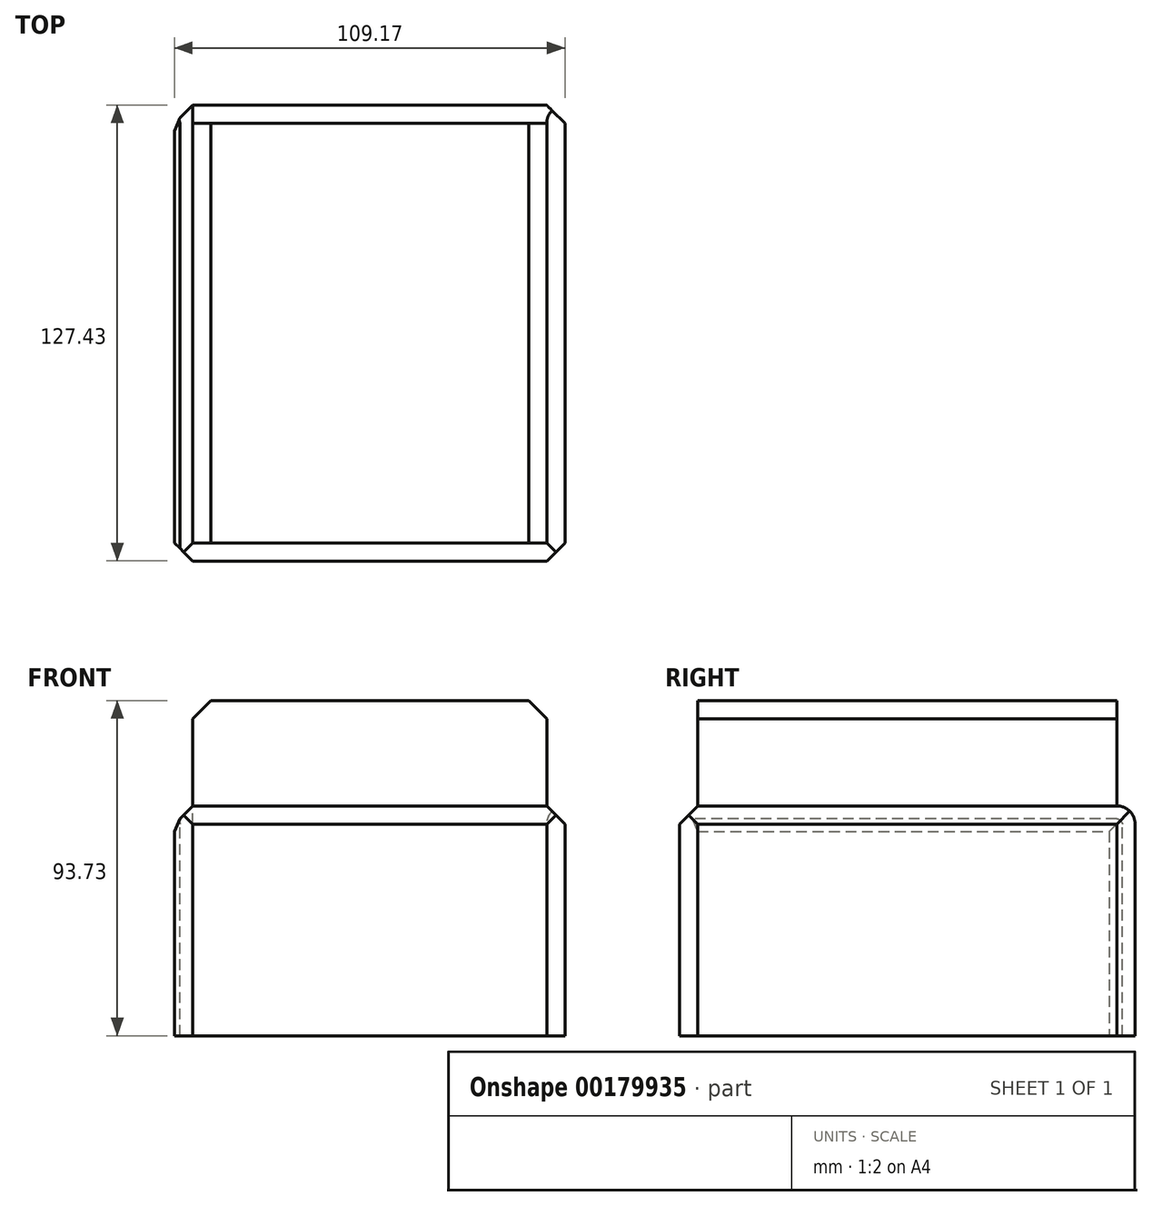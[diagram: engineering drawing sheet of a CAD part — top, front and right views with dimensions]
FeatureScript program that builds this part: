
annotation { "Feature Type Name" : "Feature", "Feature Type Description" : "" }
export const myFeature = defineFeature(function(context is Context, id is Id, definition is map)
    precondition{}
    {
        {
            var Q0;
            Q0=qCreatedBy(makeId("Top.planeOp"),FACE);
            var sketch = newSketch(context, id + "F0", { "sketchPlane" : qUnion([Q0])});
            skLineSegment(sketch, "E0.bottom", {"start": v(-52.1, 63.82) * mm, "end": v(57.08, 63.82) * mm});
            skLineSegment(sketch, "E0.top", {"start": v(-52.1, -63.61) * mm, "end": v(57.08, -63.61) * mm});
            skLineSegment(sketch, "E0.left", {"start": v(-52.1, 63.82) * mm, "end": v(-52.1, -63.61) * mm});
            skLineSegment(sketch, "E0.right", {"start": v(57.08, 63.82) * mm, "end": v(57.08, -63.61) * mm});
            skSolve(sketch);
        }
        {
            var Q0;
            Q0=makeQuery(id+"F0.imprint","IMPRINT",FACE,{"disambiguationData":[TD([[makeQuery(id+"F0.imprint","IMPRINT",EDGE,{"derivedFrom":sQuery(id+"F0.wireOp",EDGE,"E0.bottom")}),-1.0]])]});
            extrude(context, id + "F1", {"entities" : qUnion([Q0]), "depth" : 64.26 * mm});
        }
        {
            var Q0;
            Q0=makeQuery(id+"F1.opExtrude","CAP_EDGE",EDGE,{"disambiguationData":[OSD([sQuery(id+"F0.wireOp",EDGE,"E0.right")])],"isStart":false});
            chamfer(context, id + "F2", {"entities" : qUnion([Q0]), "width" : 5.08 * mm, "tangentPropagation" : true});
        }
        {
            var Q0;
            Q0=makeQuery(id+"F1.opExtrude","CAP_EDGE",EDGE,{"disambiguationData":[OSD([sQuery(id+"F0.wireOp",EDGE,"E0.bottom")])],"isStart":false});
            fillet(context, id + "F3", {"entities" : qUnion([Q0]), "radius" : 5.08 * mm, "tangentPropagation" : true, "allowEdgeOverflow" : false});
        }
        {
            var Q0;
            Q0=makeQuery(id+"F1.opExtrude","CAP_EDGE",EDGE,{"disambiguationData":[OSD([sQuery(id+"F0.wireOp",EDGE,"E0.top")])],"isStart":false});
            chamfer(context, id + "F4", {"entities" : qUnion([Q0]), "width" : 5.08 * mm, "tangentPropagation" : true});
        }
        {
            var Q0;
            Q0=makeQuery(id+"F1.opExtrude","CAP_EDGE",EDGE,{"disambiguationData":[OSD([sQuery(id+"F0.wireOp",EDGE,"E0.left")])],"isStart":false});
            chamfer(context, id + "F5", {"entities" : qUnion([Q0]), "width" : 5.08 * mm, "tangentPropagation" : true});
        }
        {
            var Q0;
            {var subQ0=sQuery(id+"F0.wireOp",EDGE,"E0.left");Q0=makeQuery(id+"F5.opChamfer","BLEND_EDGE",EDGE,{"blendedFrom":[makeQuery(id+"F1.opExtrude","SWEPT_EDGE",EDGE,{"disambiguationData":[OSD([sQuery(id+"F0.wireOp",EDGE,"E0.bottom"),subQ0])]}),makeQuery(id+"F1.opExtrude","SWEPT_FACE",FACE,{"disambiguationData":[OSD([subQ0])]})],"blendedInto":[makeQuery(id+"F1.opExtrude","SWEPT_FACE",FACE,{"disambiguationData":[OSD([subQ0])]})]});}
            chamfer(context, id + "F6", {"entities" : qUnion([Q0]), "width" : 5.08 * mm, "tangentPropagation" : true});
        }
        {
            var Q0;
            Q0=makeQuery(id+"F1.opExtrude","SWEPT_EDGE",EDGE,{"disambiguationData":[OSD([sQuery(id+"F0.wireOp",EDGE,"E0.top"),sQuery(id+"F0.wireOp",EDGE,"E0.left")])]});
            chamfer(context, id + "F7", {"entities" : qUnion([Q0]), "width" : 5.08 * mm, "tangentPropagation" : true});
        }
        {
            var Q0;
            Q0=makeQuery(id+"F1.opExtrude","SWEPT_EDGE",EDGE,{"disambiguationData":[OSD([sQuery(id+"F0.wireOp",EDGE,"E0.top"),sQuery(id+"F0.wireOp",EDGE,"E0.right")])]});
            chamfer(context, id + "F8", {"entities" : qUnion([Q0]), "width" : 5.08 * mm, "tangentPropagation" : true});
        }
        {
            var Q0;
            Q0=makeQuery(id+"F1.opExtrude","SWEPT_EDGE",EDGE,{"disambiguationData":[OSD([sQuery(id+"F0.wireOp",EDGE,"E0.bottom"),sQuery(id+"F0.wireOp",EDGE,"E0.right")])]});
            chamfer(context, id + "F9", {"entities" : qUnion([Q0]), "width" : 5.08 * mm, "tangentPropagation" : true});
        }
        {
            var Q0;
            Q0=makeQuery(id+"F1.opExtrude","CAP_FACE",FACE,{"disambiguationData":[OSD([sQuery(id+"F0.wireOp",EDGE,"E0.bottom"),sQuery(id+"F0.wireOp",EDGE,"E0.top"),sQuery(id+"F0.wireOp",EDGE,"E0.left"),sQuery(id+"F0.wireOp",EDGE,"E0.right")])],"isStart":false});
            extrude(context, id + "F10", {"entities" : qUnion([Q0]), "operationType" : NewBodyOperationType.ADD, "depth" : 29.46 * mm});
        }
        {
            var Q0;
            {var subQ0=sQuery(id+"F0.wireOp",EDGE,"E0.right");var subQ1=sQuery(id+"F0.wireOp",EDGE,"E0.left");var subQ2=sQuery(id+"F0.wireOp",EDGE,"E0.top");var subQ3=sQuery(id+"F0.wireOp",EDGE,"E0.bottom");Q0=makeQuery(id+"F10.opExtrude","CAP_EDGE",EDGE,{"disambiguationData":[OSD([subQ3,subQ2,subQ1,subQ0]),TDD([makeQuery(id+"F5.opChamfer","BLEND_EDGE",EDGE,{"blendedFrom":[makeQuery(id+"F1.opExtrude","CAP_EDGE",EDGE,{"disambiguationData":[OSD([subQ1])],"isStart":false}),makeQuery(id+"F1.opExtrude","CAP_FACE",FACE,{"disambiguationData":[OSD([subQ3,subQ2,subQ1,subQ0])],"isStart":false})],"blendedInto":[makeQuery(id+"F1.opExtrude","CAP_FACE",FACE,{"disambiguationData":[OSD([subQ3,subQ2,subQ1,subQ0])],"isStart":false})]})])],"isStart":false});}
            chamfer(context, id + "F11", {"entities" : qUnion([Q0]), "width" : 5.08 * mm, "tangentPropagation" : true});
        }
        {
            var Q0;
            {var subQ0=sQuery(id+"F0.wireOp",EDGE,"E0.right");var subQ1=sQuery(id+"F0.wireOp",EDGE,"E0.left");var subQ2=sQuery(id+"F0.wireOp",EDGE,"E0.top");var subQ3=sQuery(id+"F0.wireOp",EDGE,"E0.bottom");Q0=makeQuery(id+"F10.opExtrude","CAP_EDGE",EDGE,{"disambiguationData":[OSD([subQ3,subQ2,subQ1,subQ0]),TDD([makeQuery(id+"F2.opChamfer","BLEND_EDGE",EDGE,{"blendedFrom":[makeQuery(id+"F1.opExtrude","CAP_EDGE",EDGE,{"disambiguationData":[OSD([subQ0])],"isStart":false}),makeQuery(id+"F1.opExtrude","CAP_FACE",FACE,{"disambiguationData":[OSD([subQ3,subQ2,subQ1,subQ0])],"isStart":false})],"blendedInto":[makeQuery(id+"F1.opExtrude","CAP_FACE",FACE,{"disambiguationData":[OSD([subQ3,subQ2,subQ1,subQ0])],"isStart":false})]})])],"isStart":false});}
            chamfer(context, id + "F12", {"entities" : qUnion([Q0]), "width" : 5.08 * mm, "tangentPropagation" : true});
        }
    });
